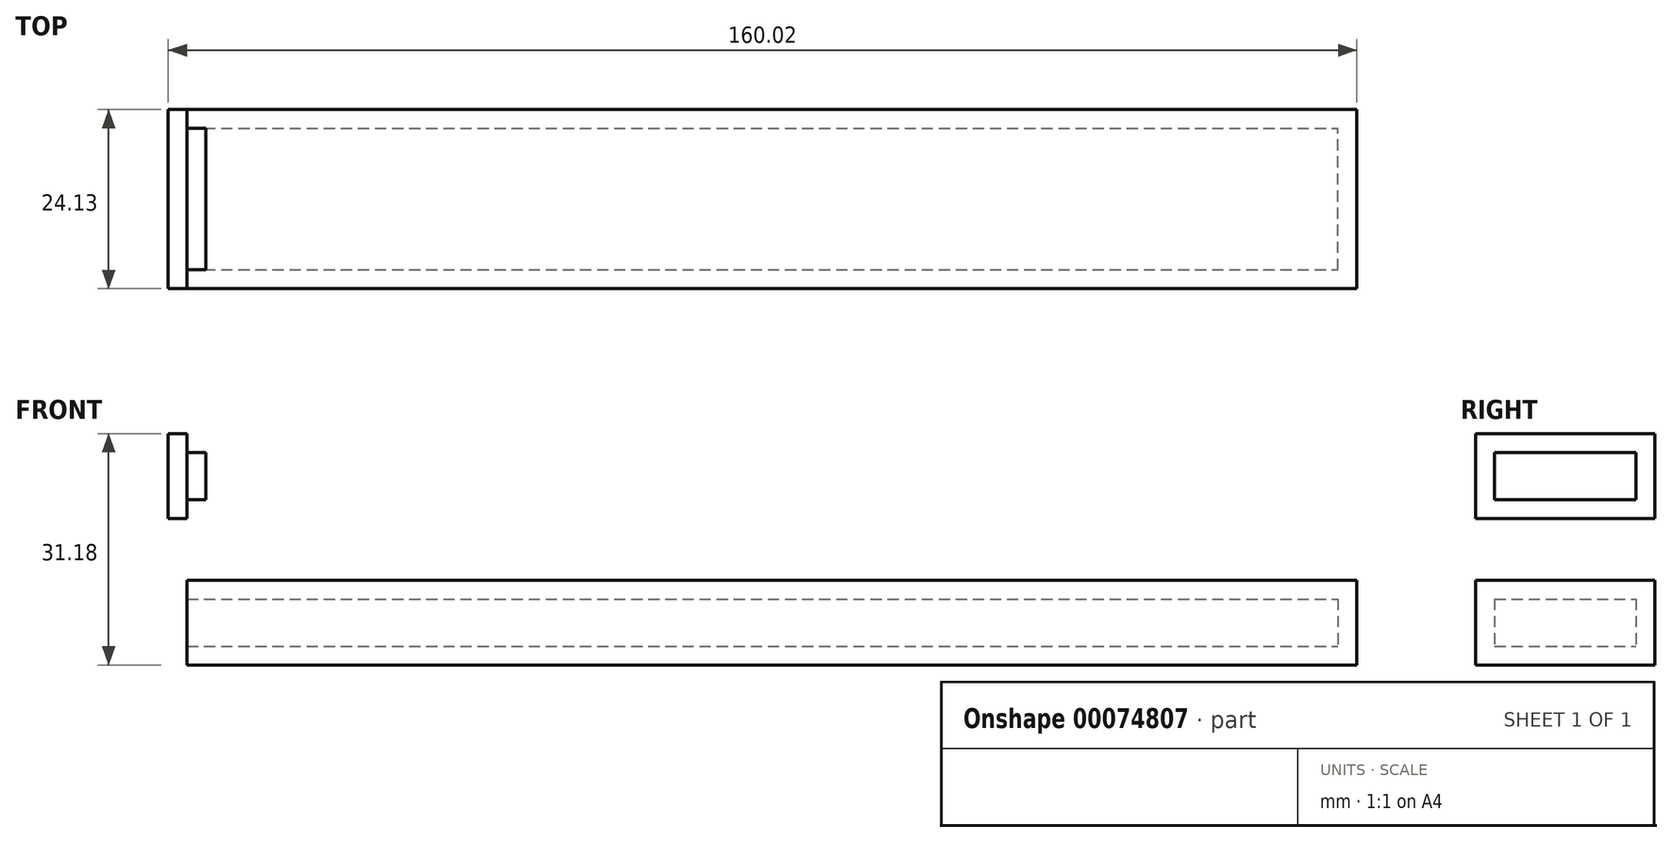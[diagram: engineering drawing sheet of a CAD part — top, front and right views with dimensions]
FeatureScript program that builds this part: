
annotation { "Feature Type Name" : "Feature", "Feature Type Description" : "" }
export const myFeature = defineFeature(function(context is Context, id is Id, definition is map)
    precondition{}
    {
        {
            var Q0;
            Q0=qCreatedBy(makeId("Top.planeOp"),FACE);
            var sketch = newSketch(context, id + "F0", { "sketchPlane" : qUnion([Q0])});
            skLineSegment(sketch, "E0.bottom", {"start": v(0, 0) * mm, "end": v(157.48, 0) * mm});
            skLineSegment(sketch, "E0.top", {"start": v(0, 24.13) * mm, "end": v(157.48, 24.13) * mm});
            skLineSegment(sketch, "E0.left", {"start": v(0, 0) * mm, "end": v(0, 24.13) * mm});
            skLineSegment(sketch, "E0.right", {"start": v(157.48, 0) * mm, "end": v(157.48, 24.13) * mm});
            skSolve(sketch);
        }
        {
            var Q0;
            Q0=makeQuery(id+"F0.imprint","IMPRINT",FACE,{"disambiguationData":[TD([[makeQuery(id+"F0.imprint","IMPRINT",EDGE,{"derivedFrom":sQuery(id+"F0.wireOp",EDGE,"E0.bottom")}),1.0]])]});
            extrude(context, id + "F1", {"entities" : qUnion([Q0]), "depth" : 11.43 * mm});
        }
        {
            var Q0;
            Q0=makeQuery(id+"F1.opExtrude","SWEPT_FACE",FACE,{"disambiguationData":[OSD([sQuery(id+"F0.wireOp",EDGE,"E0.left")])]});
            shell(context, id + "F2", {"entities" : qUnion([Q0]), "thickness" : 2.54 * mm});
        }
        {
            var Q0;
            Q0=qCreatedBy(makeId("Right.planeOp"),FACE);
            var sketch = newSketch(context, id + "F3", { "sketchPlane" : qUnion([Q0])});
            skLineSegment(sketch, "E1.bottom", {"start": v(0, 19.75) * mm, "end": v(24.13, 19.75) * mm});
            skLineSegment(sketch, "E1.top", {"start": v(0, 31.18) * mm, "end": v(24.13, 31.18) * mm});
            skLineSegment(sketch, "E1.left", {"start": v(0, 19.75) * mm, "end": v(0, 31.18) * mm});
            skLineSegment(sketch, "E1.right", {"start": v(24.13, 19.75) * mm, "end": v(24.13, 31.18) * mm});
            skLineSegment(sketch, "E2.0", {"start": v(21.6, 22.29) * mm, "end": v(21.6, 28.64) * mm});
            skLineSegment(sketch, "E2.1", {"start": v(2.54, 22.29) * mm, "end": v(21.6, 22.29) * mm});
            skLineSegment(sketch, "E2.2", {"start": v(2.54, 22.29) * mm, "end": v(2.54, 28.64) * mm});
            skLineSegment(sketch, "E2.3", {"start": v(2.54, 28.64) * mm, "end": v(21.6, 28.64) * mm});
            skSolve(sketch);
        }
        {
            var Q0;
            Q0=makeQuery(id+"F3.imprint","IMPRINT",FACE,{"disambiguationData":[TD([[makeQuery(id+"F3.imprint","IMPRINT",EDGE,{"derivedFrom":sQuery(id+"F3.wireOp",EDGE,"E1.bottom")}),1.0]])]});
            var Q1;
            Q1=makeQuery(id+"F3.imprint","IMPRINT",FACE,{"disambiguationData":[TD([[makeQuery(id+"F3.imprint","IMPRINT",EDGE,{"derivedFrom":sQuery(id+"F3.wireOp",EDGE,"E2.0")}),1.0]])]});
            extrude(context, id + "F4", {"entities" : qUnion([Q0, Q1]), "oppositeDirection" : true, "depth" : 2.54 * mm});
        }
        {
            var Q0;
            Q0=makeQuery(id+"F3.imprint","IMPRINT",FACE,{"disambiguationData":[TD([[makeQuery(id+"F3.imprint","IMPRINT",EDGE,{"derivedFrom":sQuery(id+"F3.wireOp",EDGE,"E2.0")}),1.0]])]});
            extrude(context, id + "F5", {"entities" : qUnion([Q0]), "operationType" : NewBodyOperationType.ADD, "depth" : 2.54 * mm});
        }
    });
